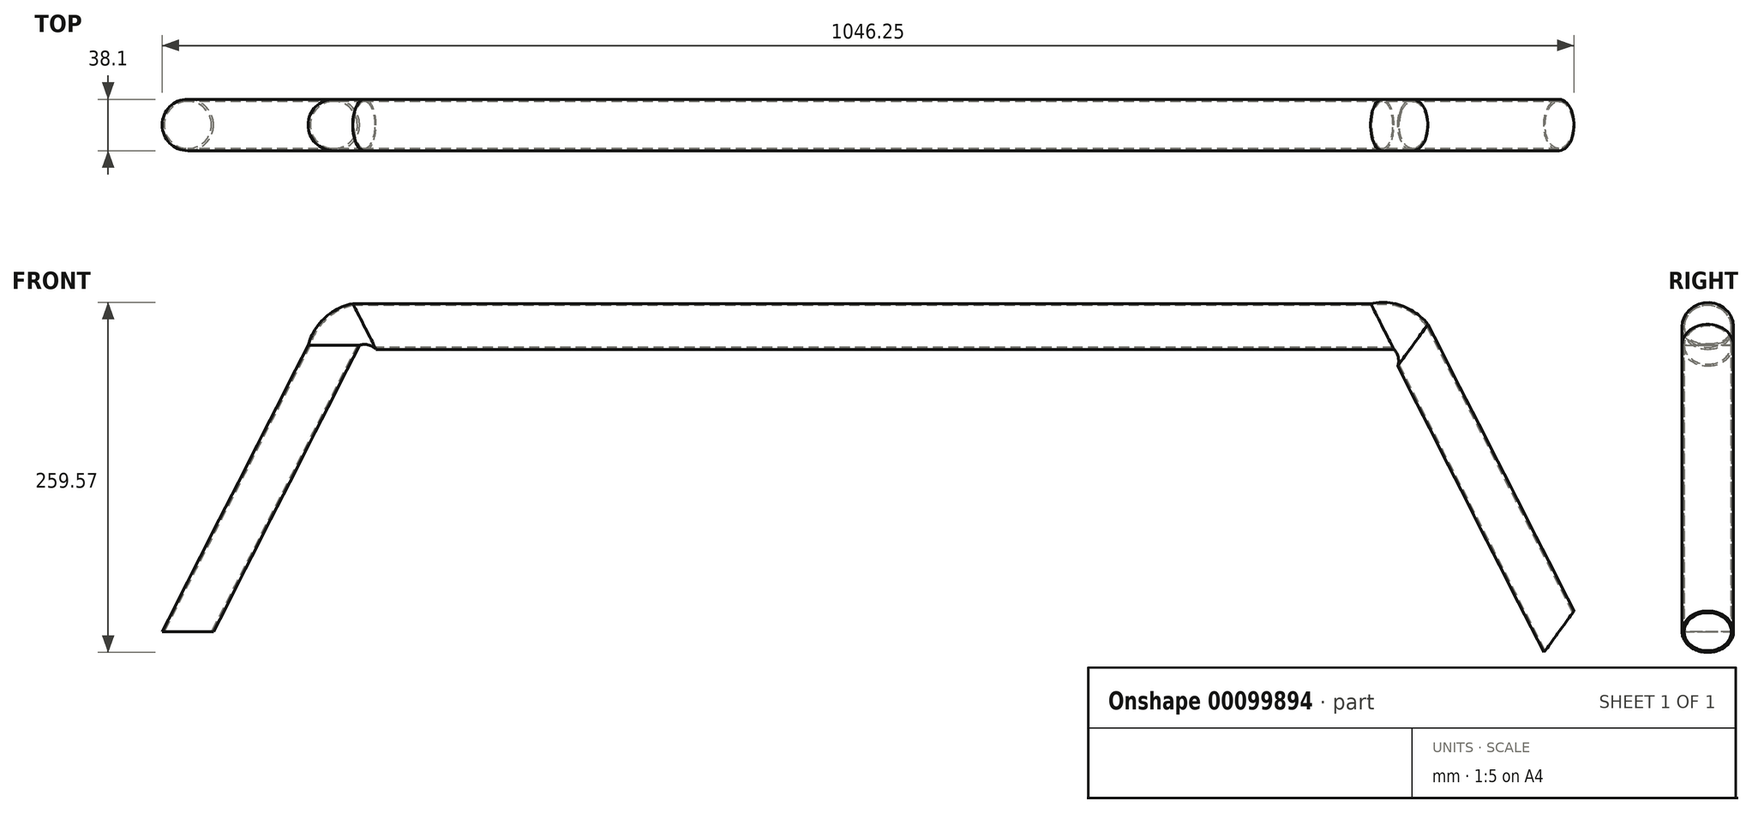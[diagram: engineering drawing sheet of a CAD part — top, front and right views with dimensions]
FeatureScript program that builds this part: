
annotation { "Feature Type Name" : "Feature", "Feature Type Description" : "" }
export const myFeature = defineFeature(function(context is Context, id is Id, definition is map)
    precondition{}
    {
        {
            var Q0;
            Q0=qCreatedBy(makeId("Top.planeOp"),FACE);
            var sketch = newSketch(context, id + "F0", { "sketchPlane" : qUnion([Q0])});
            skCircle(sketch, "E0", {"center": v(0, 0) * mm, "radius": 19.05 * mm});
            skCircle(sketch, "E1", {"center": v(0, 0) * mm, "radius": 17.46 * mm});
            skSolve(sketch);
        }
        {
            var Q0;
            Q0=qCreatedBy(makeId("Front.planeOp"),FACE);
            var sketch = newSketch(context, id + "F1", { "sketchPlane" : qUnion([Q0])});
            skLineSegment(sketch, "E2", {"start": v(0, 0) * mm, "end": v(108.25, 212.45) * mm});
            skLineSegment(sketch, "E3", {"start": v(130.88, 226.32) * mm, "end": v(885.12, 226.32) * mm});
            skLineSegment(sketch, "E4", {"start": v(907.75, 212.45) * mm, "end": v(1016, 0) * mm});
            skPoint(sketch, "E5.visualSharp", {"position": v(115.31, 226.32) * mm});
            skArc(sketch, "E5.filletArc", {"start": v(130.88, 226.32) * mm, "mid": v(117.6, 222.57) * mm, "end": v(108.25, 212.45) * mm});
            skPoint(sketch, "E6.visualSharp", {"position": v(900.69, 226.32) * mm});
            skArc(sketch, "E6.filletArc", {"start": v(907.75, 212.45) * mm, "mid": v(898.4, 222.57) * mm, "end": v(885.12, 226.32) * mm});
            skSolve(sketch);
        }
        {
            var Q0;
            Q0=makeQuery(id+"F0.imprint","IMPRINT",FACE,{"disambiguationData":[TD([[makeQuery(id+"F0.imprint","IMPRINT",EDGE,{"derivedFrom":sQuery(id+"F0.wireOp",EDGE,"E0")}),1.0]])]});
            var Q1;
            Q1=sQuery(id+"F1.wireOp",EDGE,"E2");
            var Q2;
            Q2=sQuery(id+"F1.wireOp",EDGE,"E5.filletArc");
            var Q3;
            Q3=sQuery(id+"F1.wireOp",EDGE,"E3");
            var Q4;
            Q4=sQuery(id+"F1.wireOp",EDGE,"E6.filletArc");
            var Q5;
            Q5=sQuery(id+"F1.wireOp",EDGE,"E4");
            sweep(context, id + "F2", {"profiles" : qUnion([Q0]), "path" : qUnion([Q1, Q2, Q3, Q4, Q5])});
        }
    });
